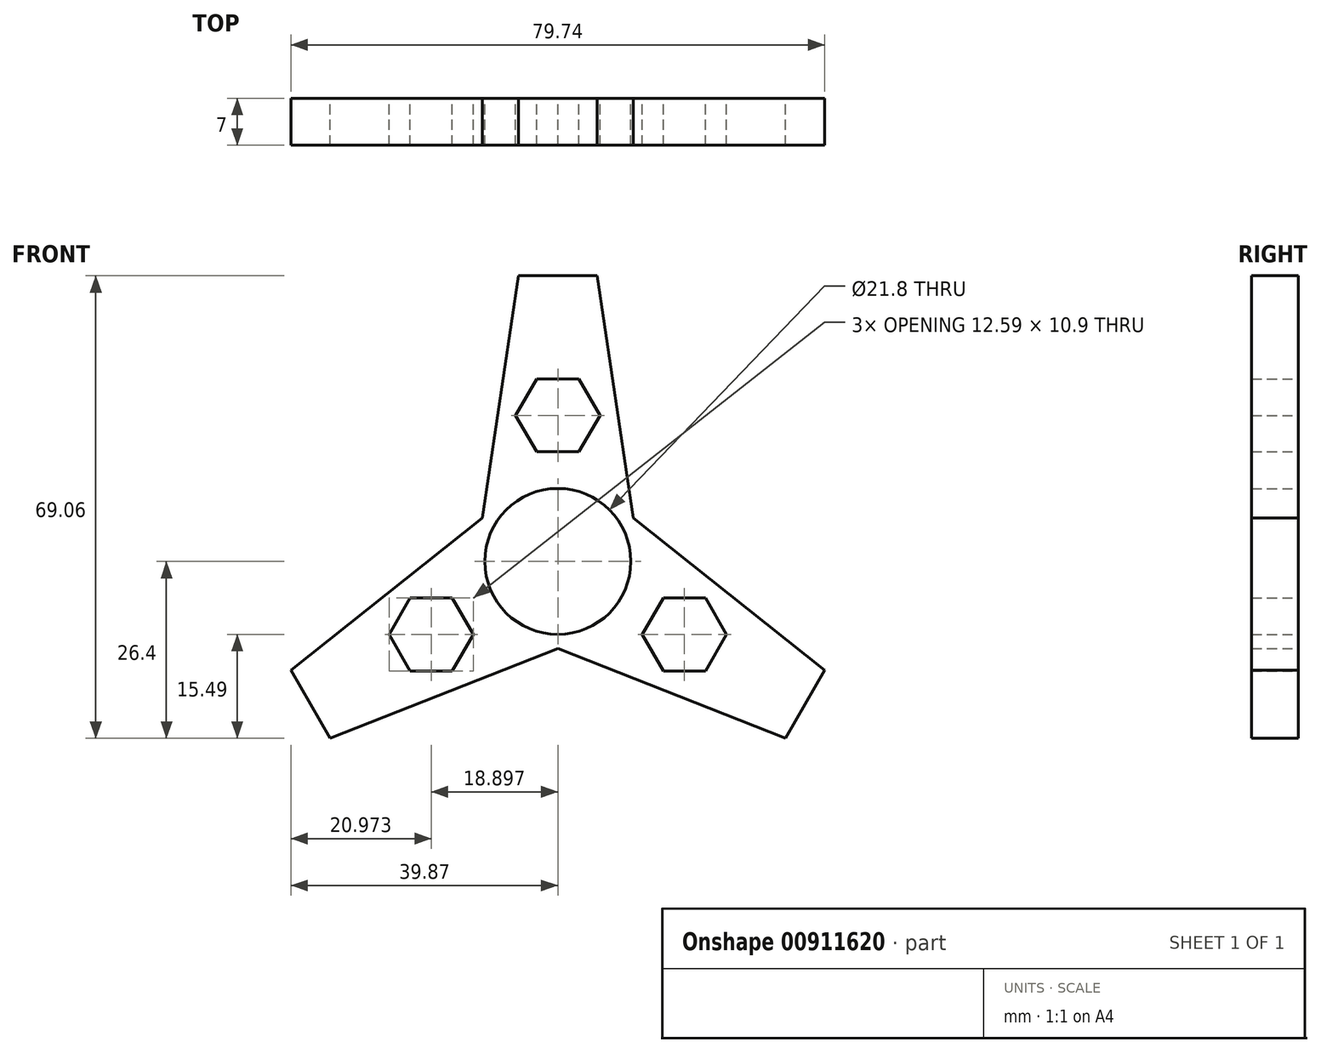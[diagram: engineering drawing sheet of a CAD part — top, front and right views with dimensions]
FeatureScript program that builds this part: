
annotation { "Feature Type Name" : "Feature", "Feature Type Description" : "" }
export const myFeature = defineFeature(function(context is Context, id is Id, definition is map)
    precondition{}
    {
        {
            var Q0;
            Q0=qCreatedBy(makeId("Front.planeOp"),FACE);
            var sketch = newSketch(context, id + "F0", { "sketchPlane" : qUnion([Q0])});
            skCircle(sketch, "E0", {"center": v(0, 0) * mm, "radius": 10.9 * mm});
            skLineSegment(sketch, "E1", {"start": v(-11.29, 6.52) * mm, "end": v(-5.86, 42.66) * mm});
            skLineSegment(sketch, "E2", {"start": v(0, 42.66) * mm, "end": v(-5.86, 42.66) * mm});
            skLineSegment(sketch, "E3.MirrorCS", {"start": v(11.29, 6.52) * mm, "end": v(5.86, 42.66) * mm});
            skLineSegment(sketch, "E4.MirrorCS", {"start": v(0, 42.66) * mm, "end": v(5.86, 42.66) * mm});
            skCircle(sketch, "E5.cCircle", {"center": v(0, 21.82) * mm, "radius": 5.45 * mm, "construction": true});
            skLineSegment(sketch, "E5.0", {"start": v(3.15, 16.37) * mm, "end": v(-3.15, 16.37) * mm});
            skLineSegment(sketch, "E5.1", {"start": v(-3.15, 16.37) * mm, "end": v(-6.3, 21.82) * mm});
            skLineSegment(sketch, "E5.2", {"start": v(-6.3, 21.82) * mm, "end": v(-3.15, 27.27) * mm});
            skLineSegment(sketch, "E5.3", {"start": v(-3.15, 27.27) * mm, "end": v(3.15, 27.27) * mm});
            skLineSegment(sketch, "E5.4", {"start": v(3.15, 27.27) * mm, "end": v(6.3, 21.82) * mm});
            skLineSegment(sketch, "E5.5", {"start": v(6.3, 21.82) * mm, "end": v(3.15, 16.37) * mm});
            skPoint(sketch, "E5.0.midPoint", {"position": v(0, 16.37) * mm});
            skCircle(sketch, "E6.1.0", {"center": v(-18.9, -10.91) * mm, "radius": 5.45 * mm, "construction": true});
            skCircle(sketch, "E6.2.0", {"center": v(18.9, -10.91) * mm, "radius": 5.45 * mm, "construction": true});
            skLineSegment(sketch, "E7.1.0", {"start": v(-22.04, -16.36) * mm, "end": v(-25.2, -10.91) * mm});
            skLineSegment(sketch, "E7.1.1", {"start": v(-15.75, -16.36) * mm, "end": v(-22.04, -16.36) * mm});
            skLineSegment(sketch, "E7.1.2", {"start": v(-12.6, -10.91) * mm, "end": v(-15.75, -16.36) * mm});
            skLineSegment(sketch, "E7.1.3", {"start": v(-15.75, -5.46) * mm, "end": v(-12.6, -10.91) * mm});
            skLineSegment(sketch, "E7.1.4", {"start": v(-22.04, -5.46) * mm, "end": v(-15.75, -5.46) * mm});
            skLineSegment(sketch, "E7.1.5", {"start": v(-25.2, -10.91) * mm, "end": v(-22.04, -5.46) * mm});
            skLineSegment(sketch, "E7.2.0", {"start": v(25.2, -10.91) * mm, "end": v(22.04, -16.36) * mm});
            skLineSegment(sketch, "E7.2.1", {"start": v(22.04, -5.46) * mm, "end": v(25.2, -10.91) * mm});
            skLineSegment(sketch, "E7.2.2", {"start": v(15.75, -5.46) * mm, "end": v(22.04, -5.46) * mm});
            skLineSegment(sketch, "E7.2.3", {"start": v(12.6, -10.91) * mm, "end": v(15.75, -5.46) * mm});
            skLineSegment(sketch, "E7.2.4", {"start": v(15.75, -16.36) * mm, "end": v(12.6, -10.91) * mm});
            skLineSegment(sketch, "E7.2.5", {"start": v(22.04, -16.36) * mm, "end": v(15.75, -16.36) * mm});
            skLineSegment(sketch, "E8.1.0", {"start": v(0, -13.04) * mm, "end": v(-34.01, -26.4) * mm});
            skLineSegment(sketch, "E8.1.1", {"start": v(-36.94, -21.33) * mm, "end": v(-34.01, -26.4) * mm});
            skLineSegment(sketch, "E8.1.2", {"start": v(-36.94, -21.33) * mm, "end": v(-39.87, -16.25) * mm});
            skLineSegment(sketch, "E8.1.3", {"start": v(-11.29, 6.52) * mm, "end": v(-39.87, -16.25) * mm});
            skLineSegment(sketch, "E8.2.0", {"start": v(11.29, 6.52) * mm, "end": v(39.87, -16.25) * mm});
            skLineSegment(sketch, "E8.2.1", {"start": v(36.94, -21.33) * mm, "end": v(39.87, -16.25) * mm});
            skLineSegment(sketch, "E8.2.2", {"start": v(36.94, -21.33) * mm, "end": v(34.01, -26.4) * mm});
            skLineSegment(sketch, "E8.2.3", {"start": v(0, -13.04) * mm, "end": v(34.01, -26.4) * mm});
            skPoint(sketch, "E9.end.orphan", {"position": v(-11.36, 6.05) * mm});
            skPoint(sketch, "E10.orphan", {"position": v(-10.92, 6.81) * mm});
            skPoint(sketch, "E11.orphan", {"position": v(-0.44, -12.86) * mm});
            skPoint(sketch, "E12.orphan", {"position": v(10.92, 6.81) * mm});
            skPoint(sketch, "E13.orphan", {"position": v(11.36, 6.05) * mm});
            skSolve(sketch);
        }
        {
            var Q0;
            Q0 = qSketchRegion(id + "F0", true);
            extrude(context, id + "F1", {"entities" : qUnion([Q0]), "depth" : 7 * mm, "offsetDistance" : 25 * mm});
        }
        {
            var Q0;
            Q0 = qSketchRegion(id + "F0", true);
            extrude(context, id + "F2", {"entities" : qUnion([Q0]), "operationType" : NewBodyOperationType.ADD, "depth" : 7 * mm, "offsetDistance" : 25 * mm});
        }
    });
